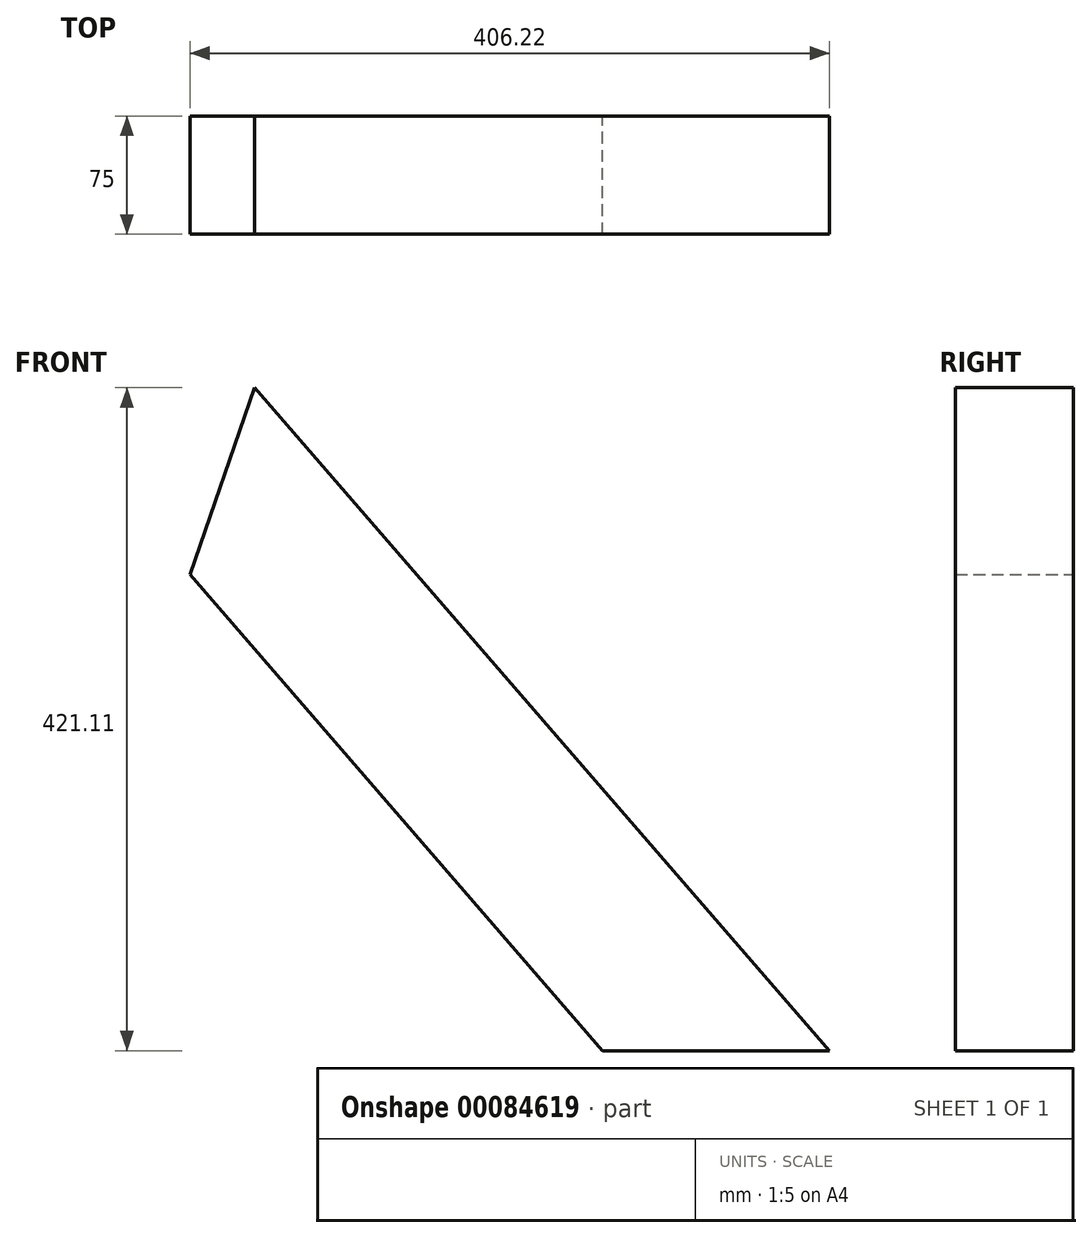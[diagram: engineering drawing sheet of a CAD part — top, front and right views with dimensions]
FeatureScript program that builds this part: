
annotation { "Feature Type Name" : "Feature", "Feature Type Description" : "" }
export const myFeature = defineFeature(function(context is Context, id is Id, definition is map)
    precondition{}
    {
        {
            var Q0;
            Q0=qCreatedBy(makeId("Front.planeOp"),FACE);
            var sketch = newSketch(context, id + "F0", { "sketchPlane" : qUnion([Q0]) });
            skLineSegment(sketch, "E0", {"start": v(-162.5, -32.08) * mm, "end": v(99.61, -334.37) * mm});
            skLineSegment(sketch, "E1", {"start": v(-162.5, -32.08) * mm, "end": v(-203.58, -150.9) * mm});
            skLineSegment(sketch, "E2", {"start": v(-203.58, -150.9) * mm, "end": v(58.54, -453.19) * mm});
            skPoint(sketch, "E3.start.orphan", {"position": v(-23.26, -358.85) * mm});
            skLineSegment(sketch, "E4", {"start": v(58.54, -453.19) * mm, "end": v(99.61, -334.37) * mm});
            skLineSegment(sketch, "E5", {"start": v(58.54, -453.19) * mm, "end": v(202.64, -453.19) * mm});
            skLineSegment(sketch, "E6", {"start": v(99.61, -334.37) * mm, "end": v(202.64, -453.19) * mm});
            skSolve(sketch);
        }
        {
            var Q0;
            Q0 = qSketchRegion(id + "F0", true);
            extrude(context, id + "F1", {"entities" : qUnion([Q0]), "endBound" : BoundingType.SYMMETRIC, "depth" : 75 * mm});
        }
    });
